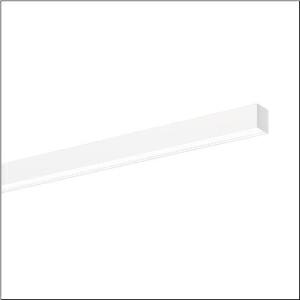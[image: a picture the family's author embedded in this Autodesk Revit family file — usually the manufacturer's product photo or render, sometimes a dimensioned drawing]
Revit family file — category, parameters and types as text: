
# Revit family: silica_r__21_51mx23da44wb_8e2d
name_source: partatom
category: Lighting Fixtures
units: mm (PartAtom-declared; Revit-internal decimal feet)

## family parameters
Cut with Voids When Loaded = No
Host = Face
Light Source = No
Part Type = Normal
Room Calculation Point = No
Round Connector Dimension = Use Diameter
Shared = No

## types (1)
- --- (1 x LED, 3280 lm, 22.4 W, 4000K)
    Apparent Load = 22 VA
    CIE Flux Codes = 78 96 99 100 100
    Color Rendering = 80
    Color Temperature = 4000K
    Default Elevation = 1800 mm
    Description = Silica® 21, office luminaire, primary optical cover: prismatic diffuser, of PMMA, CAT 2 (L<= 3000cd/m²), light emission: direct distribution, primary light characteristic: symmetric, installation type: surface-mounted, LED, rated luminous flux: 3.280lm, luminous efficacy: 146lm/W, light colour: 840, colour temperature: 4000K, with terminal, 3+2-pole, max. 2.5mm², mains connection: 220..240V, AC, 50/60Hz, rated input power: 22.4W, luminaire housing, of aluminium, traffic white (RAL 9016), length: 1.204mm, width: 53mm, height: 53mm, protection rating (complete): IP20, insulation class (complete): insulation class I (protective earthing), certification: CE, permissible operating ambient temperature: 0..+35°C, standard: EN 50419, packaging unit: 1 piece
    Height = 0 mm  [stored 0 ft]
    Lamp = 1 x LED
    Lamp Light Flux = 3280 lm
    Lamp Power = 22.4 W
    Lamp count = 1
    Length = 1204 mm
    Luminous efficacy = 146 lm/W
    Manufacturer = Siteco
    ModVariant = No
    Model = 51MX23DA44WB
    Mounting Place = Ceiling
    Mounting Type = Recessed
    Number of Poles = 1
    OnlyDefault = Yes
    Power Factor = 1
    Product Name = Silica® 21
    Product group = office luminaire | ceiling recessed
    ProductGroupID = 401
    Protection Class = Protection class I
    Protection Degree = IP 20
    RLX_Detail_Level = 1
    RLX_Emergency_Light_Flux = 0 lm
    RLX_Emergency_Type = 0
    RLX_Emergency_Type_DB = No
    RlxData = <blob elided: 18753 chars, md5=4ce8cc52>
    Socket = socket
    Standby Power = 0 W
    System Light Flux = 3280 lm
    System Power = 22 W
    Type Comments = factory setting: luminous flux: 100 % | dim-lin: 254 | 323 mA
    Type Image = l_1297777.jpg
    URL = http://relux.com
    VarID = @adj_050285
    Voltage = 0 V
    Weight = 0.00 kg
    Width = 53 mm

note: [stored X ft] marks values corroborated as IEEE doubles in the binary element streams (Revit-internal decimal feet)

## geometry (parser evidence)
native form markers: Blend x4, Sweep x11
no freeform markers — native parametric forms only
